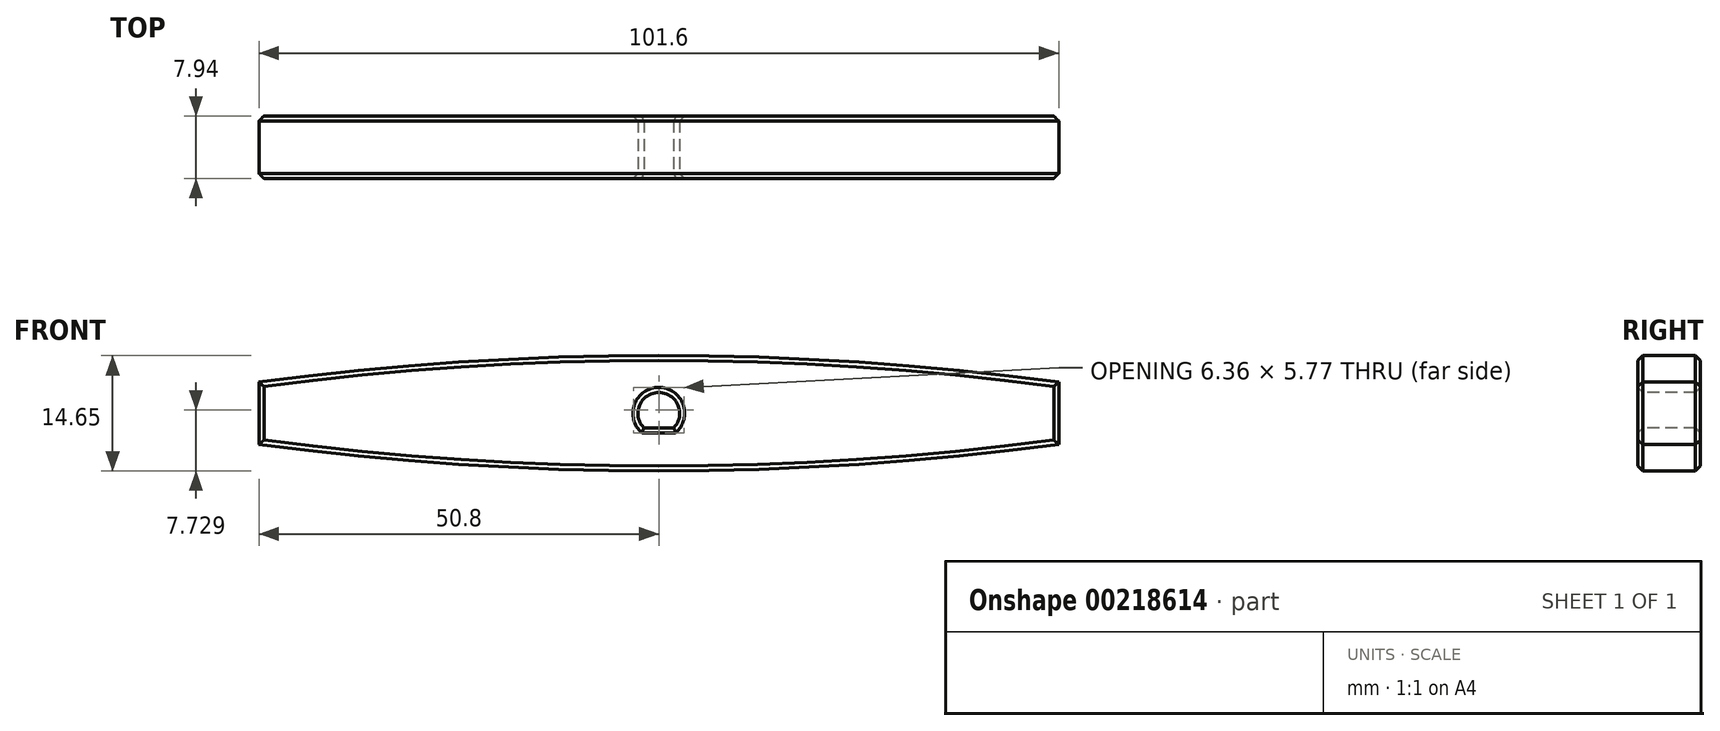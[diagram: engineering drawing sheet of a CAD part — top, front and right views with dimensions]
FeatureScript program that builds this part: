
annotation { "Feature Type Name" : "Feature", "Feature Type Description" : "" }
export const myFeature = defineFeature(function(context is Context, id is Id, definition is map)
    precondition{}
    {
        {
            var Q0;
            Q0=qCreatedBy(makeId("Front.planeOp"),FACE);
            var sketch = newSketch(context, id + "F0", { "sketchPlane" : qUnion([Q0])});
            skLineSegment(sketch, "E0", {"start": v(0, 0) * mm, "end": v(0, 7.94) * mm});
            skArc(sketch, "E1", {"start": v(101.6, 7.94) * mm, "mid": v(50.8, 11.3) * mm, "end": v(0, 7.94) * mm});
            skLineSegment(sketch, "E2", {"start": v(101.6, 7.94) * mm, "end": v(101.6, 0) * mm});
            skLineSegment(sketch, "E3", {"start": v(169.85, 3.97) * mm, "end": v(0, 3.97) * mm, "construction": true});
            skArc(sketch, "E4.MirrorCS", {"start": v(101.6, 0) * mm, "mid": v(50.8, -3.36) * mm, "end": v(0, 0) * mm});
            skSolve(sketch);
        }
        {
            var Q0;
            Q0 = qSketchRegion(id + "F0", true);
            extrude(context, id + "F1", {"entities" : qUnion([Q0]), "depth" : 7.94 * mm, "offsetDistance" : 25.4 * mm});
        }
        {
            var Q0;
            Q0=makeQuery(id+"F1.opExtrude","CAP_FACE",FACE,{"disambiguationData":[OSD([sQuery(id+"F0.wireOp",EDGE,"E0"),sQuery(id+"F0.wireOp",EDGE,"E1"),sQuery(id+"F0.wireOp",EDGE,"E2"),sQuery(id+"F0.wireOp",EDGE,"E4.MirrorCS")])],"isStart":false});
            var sketch = newSketch(context, id + "F2", { "sketchPlane" : qUnion([Q0])});
            skArc(sketch, "E5", {"start": v(52.7, 2.12) * mm, "mid": v(50.8, 6.62) * mm, "end": v(48.9, 2.12) * mm});
            skLineSegment(sketch, "E6", {"start": v(0, 3.97) * mm, "end": v(101.6, 3.97) * mm, "construction": true});
            skLineSegment(sketch, "E7", {"start": v(48.9, 2.12) * mm, "end": v(52.7, 2.12) * mm});
            skSolve(sketch);
        }
        {
            var Q0;
            Q0 = qSketchRegion(id + "F2", true);
            extrude(context, id + "F3", {"entities" : qUnion([Q0]), "operationType" : NewBodyOperationType.REMOVE, "endBound" : BoundingType.THROUGH_ALL, "oppositeDirection" : true, "depth" : 25.4 * mm, "offsetDistance" : 25.4 * mm});
        }
        {
            var Q0;
            Q0=makeQuery(id+"F1.opExtrude","CAP_FACE",FACE,{"disambiguationData":[OSD([sQuery(id+"F0.wireOp",EDGE,"E0"),sQuery(id+"F0.wireOp",EDGE,"E1"),sQuery(id+"F0.wireOp",EDGE,"E2"),sQuery(id+"F0.wireOp",EDGE,"E4.MirrorCS")])],"isStart":false});
            var Q1;
            Q1=makeQuery(id+"F1.opExtrude","CAP_FACE",FACE,{"disambiguationData":[OSD([sQuery(id+"F0.wireOp",EDGE,"E0"),sQuery(id+"F0.wireOp",EDGE,"E1"),sQuery(id+"F0.wireOp",EDGE,"E2"),sQuery(id+"F0.wireOp",EDGE,"E4.MirrorCS")])],"isStart":true});
            chamfer(context, id + "F4", {"entities" : qUnion([Q0, Q1]), "width" : 0.64 * mm, "tangentPropagation" : true});
        }
    });
